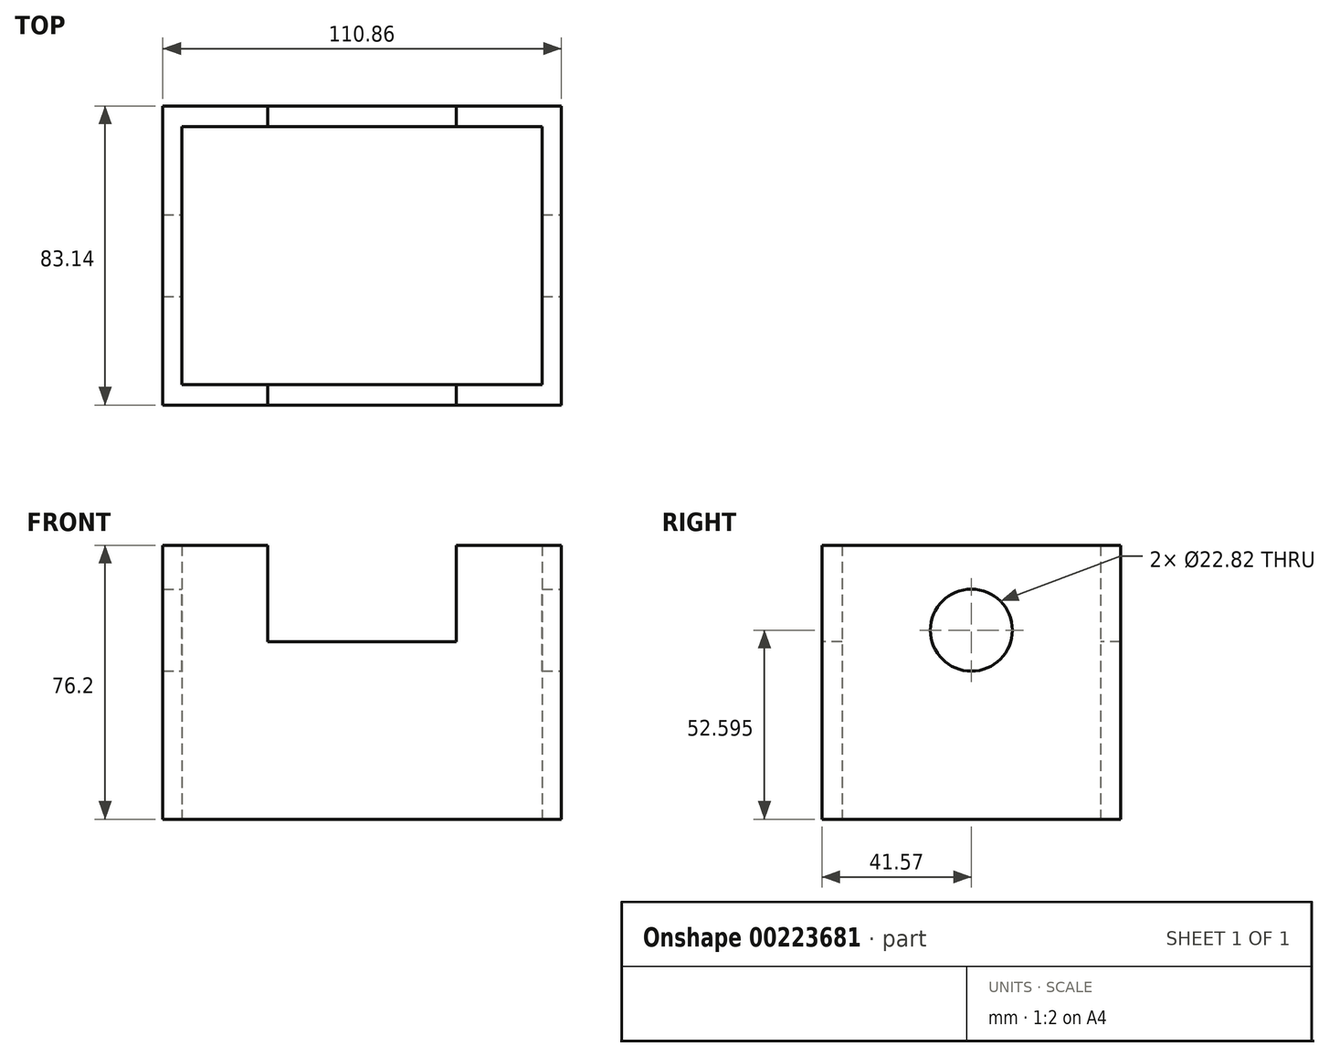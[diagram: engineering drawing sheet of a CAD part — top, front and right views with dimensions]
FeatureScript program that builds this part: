
annotation { "Feature Type Name" : "Feature", "Feature Type Description" : "" }
export const myFeature = defineFeature(function(context is Context, id is Id, definition is map)
    precondition{}
    {
        {
            var Q0;
            Q0=qCreatedBy(makeId("Top.planeOp"),FACE);
            var sketch = newSketch(context, id + "F0", { "sketchPlane" : qUnion([Q0])});
            skLineSegment(sketch, "E0.bottom", {"start": v(-55.43, 41.57) * mm, "end": v(55.43, 41.57) * mm});
            skLineSegment(sketch, "E0.top", {"start": v(-55.43, -41.57) * mm, "end": v(55.43, -41.57) * mm});
            skLineSegment(sketch, "E0.left", {"start": v(-55.43, 41.57) * mm, "end": v(-55.43, -41.57) * mm});
            skLineSegment(sketch, "E0.right", {"start": v(55.43, 41.57) * mm, "end": v(55.43, -41.57) * mm});
            skPoint(sketch, "E0.middle", {"position": v(0, 0) * mm});
            skLineSegment(sketch, "E1.bottom", {"start": v(-50.06, 35.9) * mm, "end": v(50.06, 35.9) * mm});
            skLineSegment(sketch, "E1.top", {"start": v(-50.06, -35.9) * mm, "end": v(50.06, -35.9) * mm});
            skLineSegment(sketch, "E1.left", {"start": v(-50.06, 35.9) * mm, "end": v(-50.06, -35.9) * mm});
            skLineSegment(sketch, "E1.right", {"start": v(50.06, 35.9) * mm, "end": v(50.06, -35.9) * mm});
            skSolve(sketch);
        }
        {
            var Q0;
            Q0 = qSketchRegion(id + "F0", true);
            extrude(context, id + "F1", {"entities" : qUnion([Q0]), "depth" : 76.2 * mm});
        }
        {
            var Q0;
            Q0=makeQuery(id+"F1.opExtrude","SWEPT_FACE",FACE,{"disambiguationData":[OSD([sQuery(id+"F0.wireOp",EDGE,"E0.top")])]});
            var sketch = newSketch(context, id + "F2", { "sketchPlane" : qUnion([Q0])});
            skLineSegment(sketch, "E2.bottom", {"start": v(-26.22, 49.32) * mm, "end": v(26.22, 49.32) * mm});
            skLineSegment(sketch, "E2.top", {"start": v(-26.22, 103.08) * mm, "end": v(26.22, 103.08) * mm});
            skLineSegment(sketch, "E2.left", {"start": v(-26.22, 49.32) * mm, "end": v(-26.22, 103.08) * mm});
            skLineSegment(sketch, "E2.right", {"start": v(26.22, 49.32) * mm, "end": v(26.22, 103.08) * mm});
            skPoint(sketch, "E2.middle", {"position": v(0, 76.2) * mm});
            skSolve(sketch);
        }
        {
            var Q0;
            {var subQ0=sQuery(id+"F2.wireOp",EDGE,"E2.bottom");Q0=makeQuery(id+"F2.imprint","IMPRINT",FACE,{"disambiguationData":[TD([[makeQuery(id+"F2.imprint","IMPRINT",EDGE,{"derivedFrom":subQ0}),1.0]])]});}
            extrude(context, id + "F3", {"entities" : qUnion([Q0]), "operationType" : NewBodyOperationType.REMOVE, "oppositeDirection" : true, "depth" : 103.12 * mm});
        }
        {
            var Q0;
            Q0=makeQuery(id+"F1.opExtrude","SWEPT_FACE",FACE,{"disambiguationData":[OSD([sQuery(id+"F0.wireOp",EDGE,"E0.right")])]});
            var sketch = newSketch(context, id + "F4", { "sketchPlane" : qUnion([Q0])});
            skCircle(sketch, "E3", {"center": v(0, 52.6) * mm, "radius": 11.4 * mm});
            skSolve(sketch);
        }
        {
            var Q0;
            Q0=makeQuery(id+"F4.imprint","IMPRINT",FACE,{"disambiguationData":[TD([[makeQuery(id+"F4.imprint","IMPRINT",EDGE,{"derivedFrom":sQuery(id+"F4.wireOp",EDGE,"E3")}),1.0]])]});
            extrude(context, id + "F5", {"entities" : qUnion([Q0]), "operationType" : NewBodyOperationType.REMOVE, "oppositeDirection" : true, "depth" : 113.54 * mm});
        }
    });
